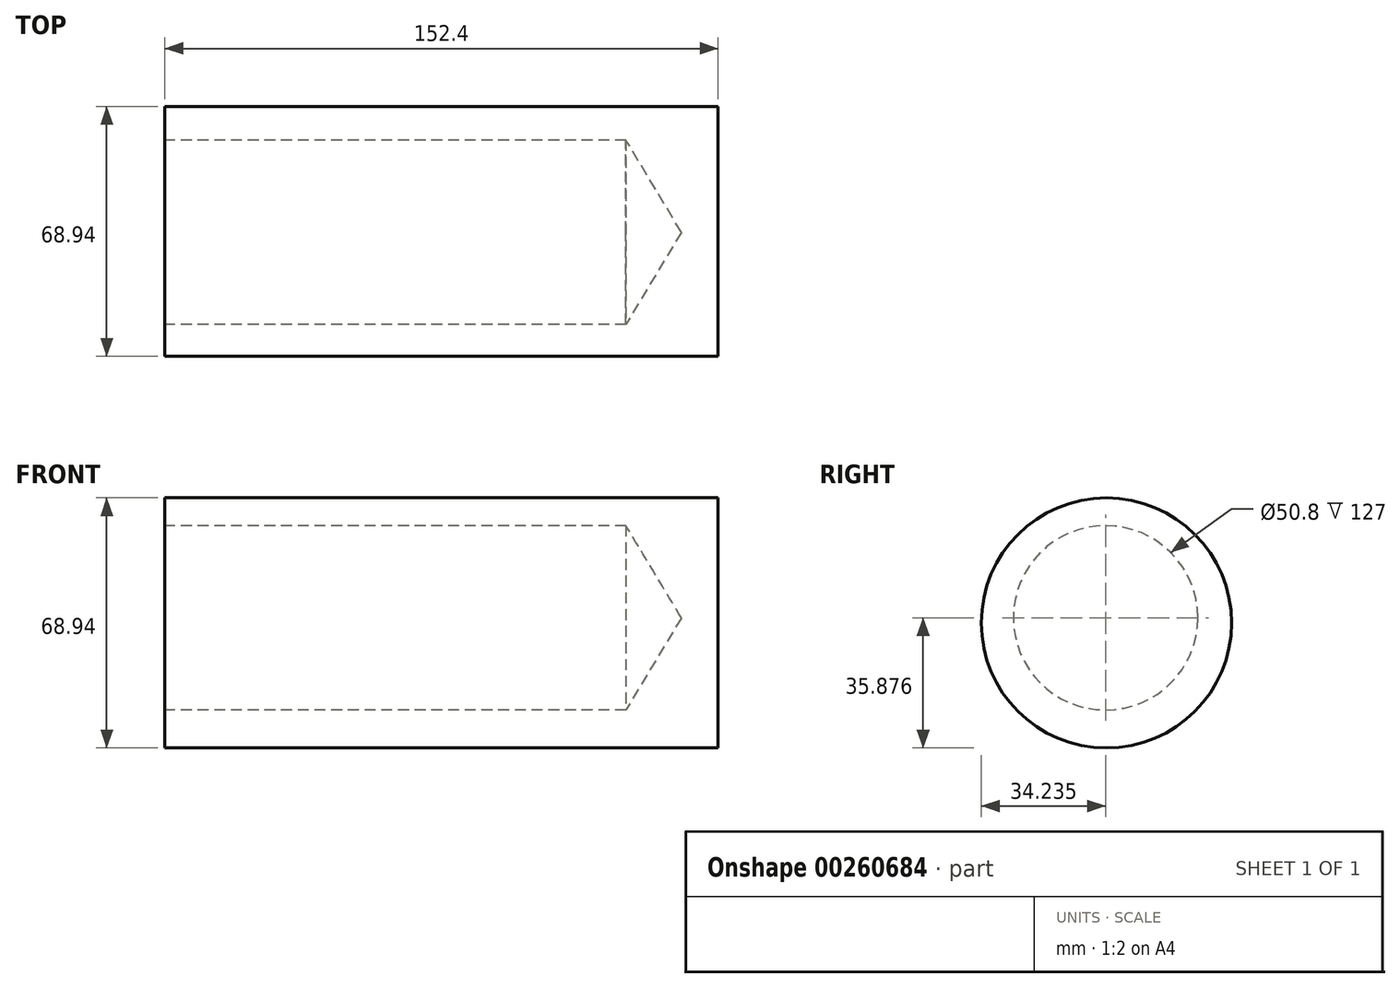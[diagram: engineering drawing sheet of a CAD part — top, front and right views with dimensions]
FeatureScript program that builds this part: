
annotation { "Feature Type Name" : "Feature", "Feature Type Description" : "" }
export const myFeature = defineFeature(function(context is Context, id is Id, definition is map)
    precondition{}
    {
        {
            var Q0;
            Q0=qCreatedBy(makeId("Right.planeOp"),FACE);
            var sketch = newSketch(context, id + "F0", { "sketchPlane" : qUnion([Q0])});
            skCircle(sketch, "E0", {"center": v(-24.6, 23.78) * mm, "radius": 34.47 * mm});
            skSolve(sketch);
        }
        {
            var Q0;
            Q0=makeQuery(id+"F0.imprint","IMPRINT",FACE,{"disambiguationData":[TD([[makeQuery(id+"F0.imprint","IMPRINT",EDGE,{"derivedFrom":sQuery(id+"F0.wireOp",EDGE,"E0")}),1.0]])]});
            extrude(context, id + "F1", {"entities" : qUnion([Q0]), "depth" : 152.4 * mm});
        }
        {
            var Q0;
            Q0=qCreatedBy(makeId("Right.planeOp"),FACE);
            var sketch = newSketch(context, id + "F2", { "sketchPlane" : qUnion([Q0])});
            skLineSegment(sketch, "E1.bottom", {"start": v(-24.83, 25.19) * mm, "end": v(47.8, 25.19) * mm});
            skLineSegment(sketch, "E1.top", {"start": v(-24.83, -33.85) * mm, "end": v(47.8, -33.85) * mm});
            skLineSegment(sketch, "E1.left", {"start": v(-24.83, 25.19) * mm, "end": v(-24.83, -33.85) * mm});
            skLineSegment(sketch, "E1.right", {"start": v(47.8, 25.19) * mm, "end": v(47.8, -33.85) * mm});
            skSolve(sketch);
        }
        {
            var Q0;
            Q0=sQuery(id+"F2.wireOp",VERTEX,"E1.left.start");
            var Q1;
            Q1=makeQuery(id+"F1.opExtrude","SWEPT_BODY",BODY,{"disambiguationData":[OSD([sQuery(id+"F0.wireOp",EDGE,"E0")])]});
            hole(context, id + "F3", {"style" : HoleStyle.SIMPLE, "endStyle" : HoleEndStyle.BLIND, "oppositeDirection" : true, "holeDiameter" : 50.8 * mm, "holeDepth" : 127 * mm, "tappedDepth" : 12.7 * mm, "tapClearance" : 3, "locations" : qUnion([Q0]), "scope" : qUnion([Q1])});
        }
    });
